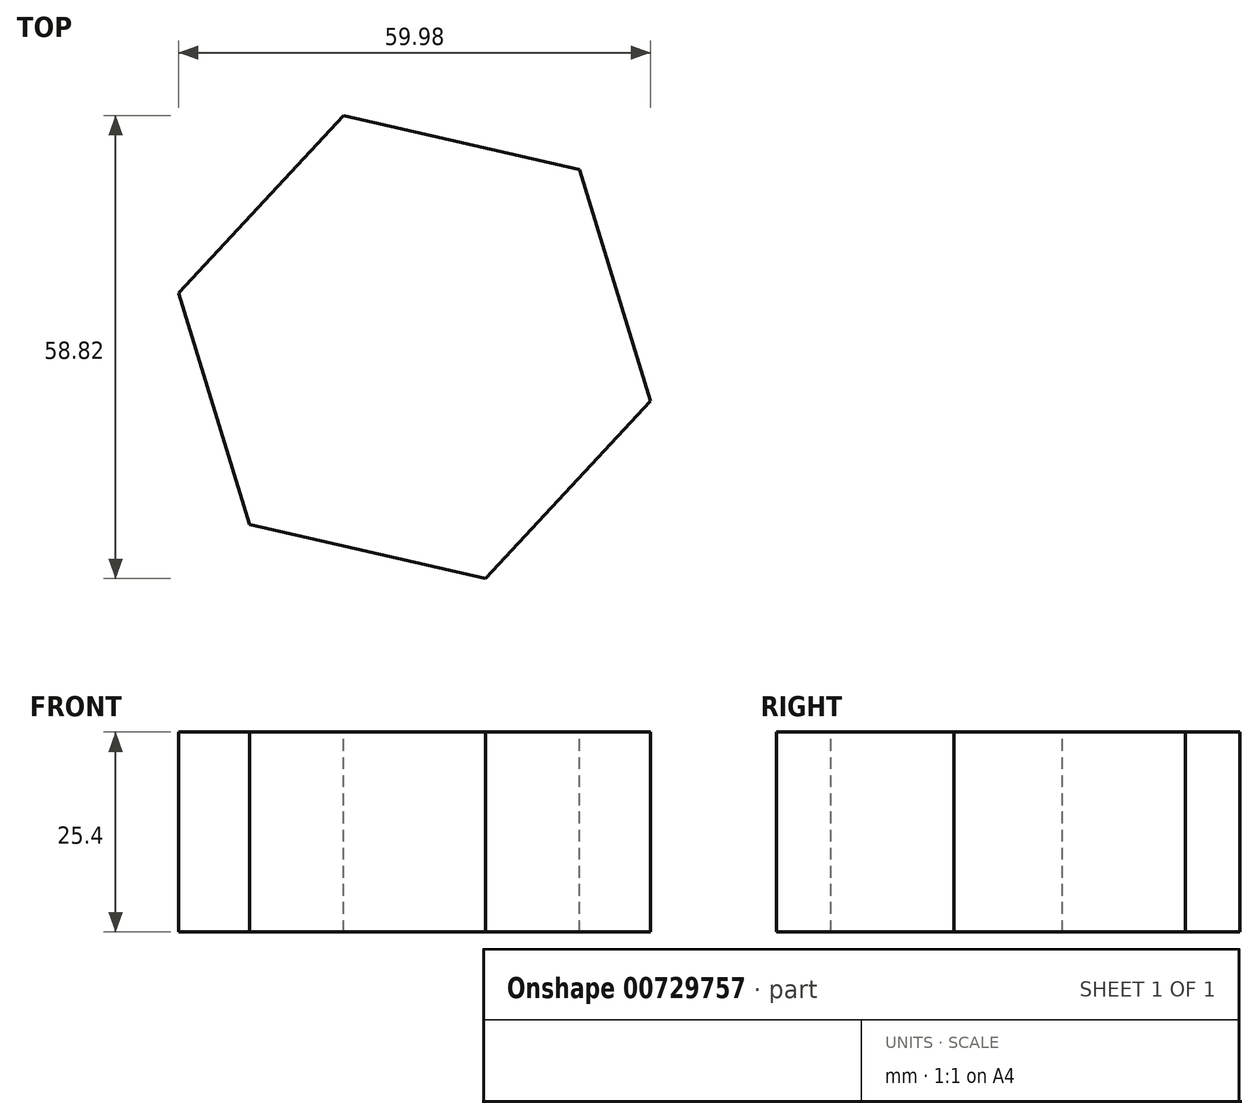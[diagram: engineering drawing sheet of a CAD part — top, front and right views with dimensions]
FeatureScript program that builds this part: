
annotation { "Feature Type Name" : "Feature", "Feature Type Description" : "" }
export const myFeature = defineFeature(function(context is Context, id is Id, definition is map)
    precondition{}
    {
        {
            var Q0;
            Q0=qCreatedBy(makeId("Top.planeOp"),FACE);
            var sketch = newSketch(context, id + "F0", { "sketchPlane" : qUnion([Q0])});
            skCircle(sketch, "E0.cCircle", {"center": v(0, 0) * mm, "radius": 26.65 * mm, "construction": true});
            skLineSegment(sketch, "E0.0", {"start": v(29.99, -6.89) * mm, "end": v(9.03, -29.41) * mm});
            skLineSegment(sketch, "E0.1", {"start": v(9.03, -29.41) * mm, "end": v(-20.96, -22.53) * mm});
            skLineSegment(sketch, "E0.2", {"start": v(-20.96, -22.53) * mm, "end": v(-29.99, 6.89) * mm});
            skLineSegment(sketch, "E0.3", {"start": v(-29.99, 6.89) * mm, "end": v(-9.03, 29.41) * mm});
            skLineSegment(sketch, "E0.4", {"start": v(-9.03, 29.41) * mm, "end": v(20.96, 22.53) * mm});
            skLineSegment(sketch, "E0.5", {"start": v(20.96, 22.53) * mm, "end": v(29.99, -6.89) * mm});
            skPoint(sketch, "E0.0.midPoint", {"position": v(19.51, -18.15) * mm});
            skSolve(sketch);
        }
        {
            var Q0;
            Q0 = qSketchRegion(id + "F0", true);
            extrude(context, id + "F1", {"entities" : qUnion([Q0]), "oppositeDirection" : true, "depth" : 25.4 * mm, "offsetDistance" : 25.4 * mm});
        }
    });
